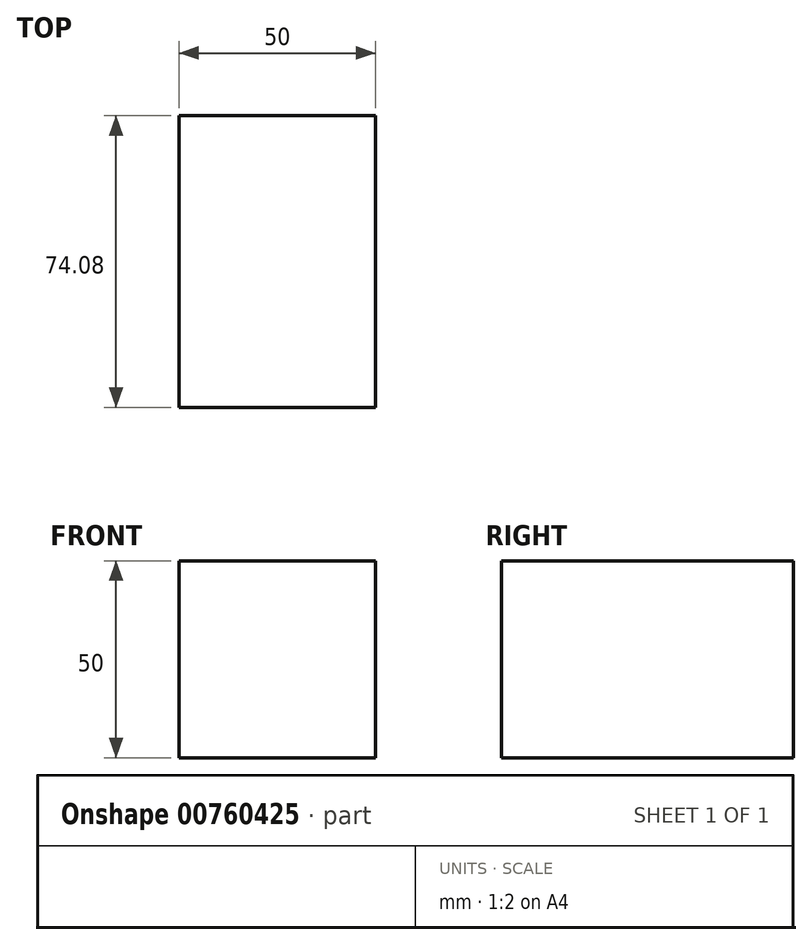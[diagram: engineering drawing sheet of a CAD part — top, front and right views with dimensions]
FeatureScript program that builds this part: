
annotation { "Feature Type Name" : "Feature", "Feature Type Description" : "" }
export const myFeature = defineFeature(function(context is Context, id is Id, definition is map)
    precondition{}
    {
        {
            assignVariable(context, id + "F0", {"name" : "MASS", "anyValue" : 1435});
        }
        {
            var Q0;
            Q0=qCreatedBy(makeId("Front.planeOp"),FACE);
            var sketch = newSketch(context, id + "F1", { "sketchPlane" : qUnion([Q0])});
            skLineSegment(sketch, "E0.bottom", {"start": v(-25, 25) * mm, "end": v(25, 25) * mm});
            skLineSegment(sketch, "E0.top", {"start": v(-25, -25) * mm, "end": v(25, -25) * mm});
            skLineSegment(sketch, "E0.left", {"start": v(-25, 25) * mm, "end": v(-25, -25) * mm});
            skLineSegment(sketch, "E0.right", {"start": v(25, 25) * mm, "end": v(25, -25) * mm});
            skSolve(sketch);
        }
        {
            var Q0;
            Q0=makeQuery(id+"F1.imprint","IMPRINT",FACE,{"disambiguationData":[TD([[makeQuery(id+"F1.imprint","IMPRINT",EDGE,{"derivedFrom":sQuery(id+"F1.wireOp",EDGE,"E0.bottom")}),-1.0]])]});
            extrude(context, id + "F2", {"entities" : qUnion([Q0]), "endBound" : BoundingType.SYMMETRIC, "depth" : (getVariable(context, 'MASS') / 19.37) * mm, "offsetDistance" : 25 * mm});
        }
    });
